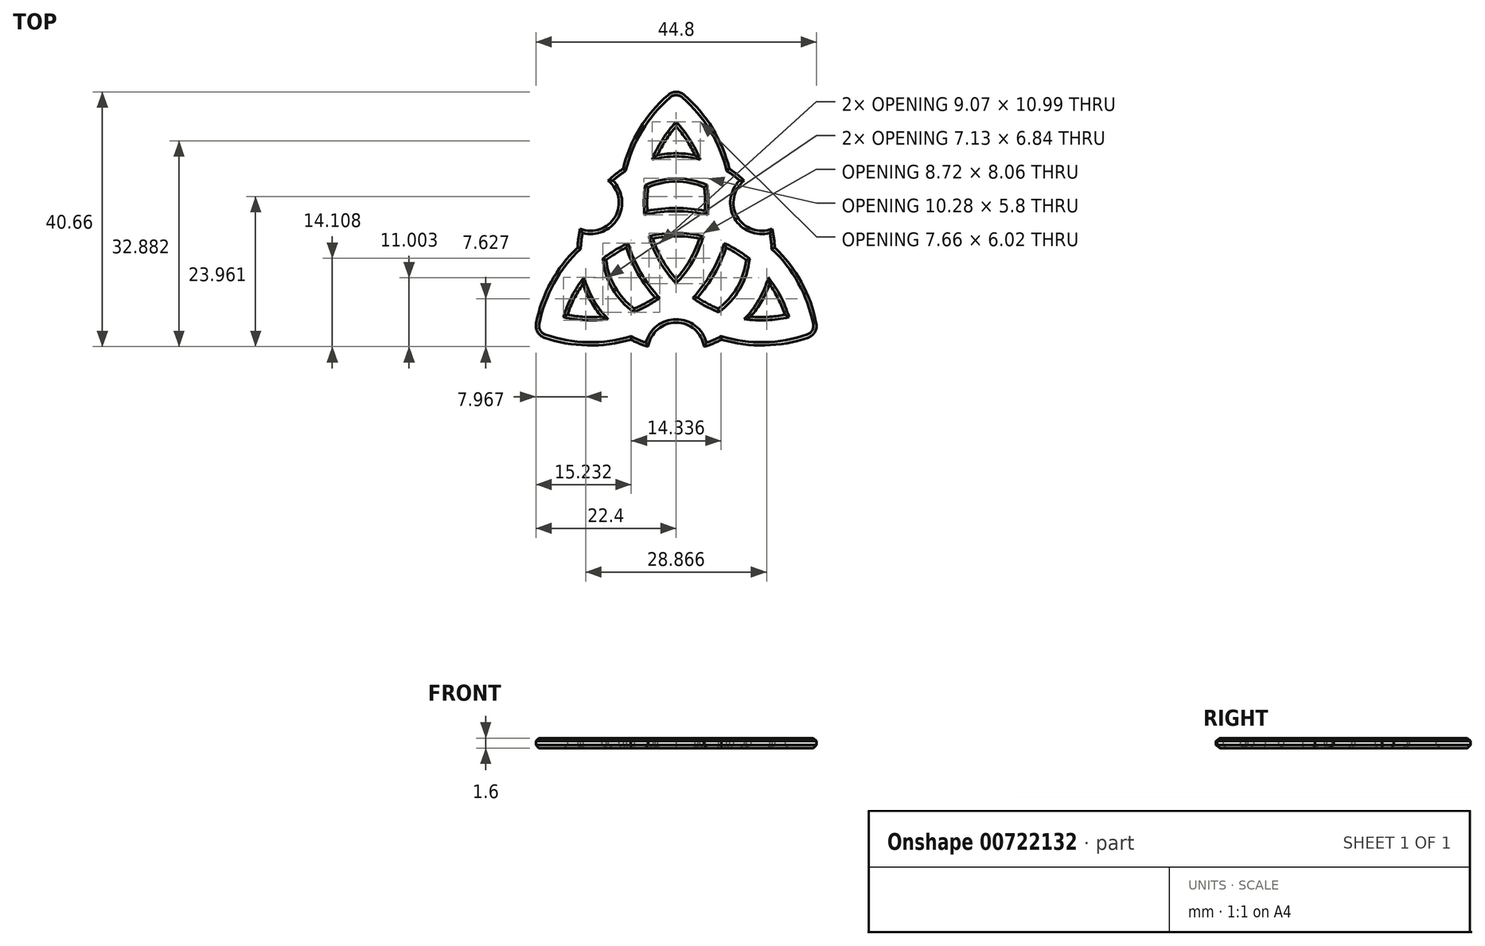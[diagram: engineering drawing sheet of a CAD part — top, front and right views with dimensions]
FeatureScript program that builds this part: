
annotation { "Feature Type Name" : "Feature", "Feature Type Description" : "" }
export const myFeature = defineFeature(function(context is Context, id is Id, definition is map)
    precondition{}
    {
        {
            var Q0;
            Q0=qCreatedBy(makeId("Top.planeOp"),FACE);
            var sketch = newSketch(context, id + "F0", { "sketchPlane" : qUnion([Q0])});
            skCircle(sketch, "E0", {"center": v(0, 0) * mm, "radius": 15.75 * mm});
            skCircle(sketch, "E1", {"center": v(0, 0) * mm, "radius": 11.25 * mm});
            skCircle(sketch, "E2", {"center": v(13.64, 7.88) * mm, "radius": 4.5 * mm});
            skCircle(sketch, "E3.1.0", {"center": v(-13.64, 7.88) * mm, "radius": 4.5 * mm});
            skCircle(sketch, "E3.2.0", {"center": v(0, -15.75) * mm, "radius": 4.5 * mm});
            skLineSegment(sketch, "E4", {"start": v(0, 0) * mm, "end": v(13.64, 7.88) * mm, "construction": true});
            skCircle(sketch, "E5", {"center": v(13.64, 7.88) * mm, "radius": 22.78 * mm});
            skCircle(sketch, "E6", {"center": v(13.64, 7.88) * mm, "radius": 18.28 * mm});
            skCircle(sketch, "E7.1.0", {"center": v(-13.64, 7.88) * mm, "radius": 18.28 * mm});
            skCircle(sketch, "E7.1.1", {"center": v(-13.64, 7.88) * mm, "radius": 22.78 * mm});
            skCircle(sketch, "E7.2.0", {"center": v(0, -15.75) * mm, "radius": 18.28 * mm});
            skCircle(sketch, "E7.2.1", {"center": v(0, -15.75) * mm, "radius": 22.78 * mm});
            skSolve(sketch);
        }
        {
            var Q0;
            {var subQ0=sQuery(id+"F0.wireOp",EDGE,"E7.2.0");var subQ1=sQuery(id+"F0.wireOp",EDGE,"E7.1.0");var subQ2=makeQuery(id+"F0.imprint","INTERSECT",VERTEX,{"disambiguationData":[OD(1.0)],"derivedFrom":[subQ1,subQ0]});Q0=makeQuery(id+"F0.imprint","IMPRINT",FACE,{"disambiguationData":[TD([[makeQuery(id+"F0.imprint","IMPRINT",EDGE,{"disambiguationData":[TD([[subQ2,-1.0]])],"derivedFrom":subQ1}),-1.0]])]});}
            var Q1;
            {var subQ0=sQuery(id+"F0.wireOp",EDGE,"E7.2.1");var subQ1=sQuery(id+"F0.wireOp",EDGE,"E1");var subQ2=makeQuery(id+"F0.imprint","INTERSECT",VERTEX,{"disambiguationData":[OD(0.0)],"derivedFrom":[subQ1,subQ0]});Q1=makeQuery(id+"F0.imprint","IMPRINT",FACE,{"disambiguationData":[TD([[makeQuery(id+"F0.imprint","IMPRINT",EDGE,{"disambiguationData":[TD([[subQ2,1.0]])],"derivedFrom":subQ1}),1.0]])]});}
            var Q2;
            {var subQ0=sQuery(id+"F0.wireOp",EDGE,"E7.2.1");var subQ1=sQuery(id+"F0.wireOp",EDGE,"E0");var subQ2=makeQuery(id+"F0.imprint","INTERSECT",VERTEX,{"disambiguationData":[OD(0.0)],"derivedFrom":[subQ1,subQ0]});Q2=makeQuery(id+"F0.imprint","IMPRINT",FACE,{"disambiguationData":[TD([[makeQuery(id+"F0.imprint","IMPRINT",EDGE,{"disambiguationData":[TD([[subQ2,1.0]])],"derivedFrom":subQ1}),1.0]])]});}
            var Q3;
            {var subQ0=sQuery(id+"F0.wireOp",EDGE,"E7.2.1");var subQ1=sQuery(id+"F0.wireOp",EDGE,"E0");var subQ2=makeQuery(id+"F0.imprint","INTERSECT",VERTEX,{"disambiguationData":[OD(0.0)],"derivedFrom":[subQ1,subQ0]});Q3=makeQuery(id+"F0.imprint","IMPRINT",FACE,{"disambiguationData":[TD([[makeQuery(id+"F0.imprint","IMPRINT",EDGE,{"disambiguationData":[TD([[subQ2,1.0]])],"derivedFrom":subQ1}),-1.0]])]});}
            var Q4;
            {var subQ0=sQuery(id+"F0.wireOp",EDGE,"E7.2.1");var subQ1=sQuery(id+"F0.wireOp",EDGE,"E5");var subQ2=makeQuery(id+"F0.imprint","INTERSECT",VERTEX,{"disambiguationData":[OD(0.0)],"derivedFrom":[subQ1,subQ0]});Q4=makeQuery(id+"F0.imprint","IMPRINT",FACE,{"disambiguationData":[TD([[makeQuery(id+"F0.imprint","IMPRINT",EDGE,{"disambiguationData":[TD([[subQ2,1.0]])],"derivedFrom":subQ1}),1.0]])]});}
            var Q5;
            {var subQ0=sQuery(id+"F0.wireOp",EDGE,"E5");var subQ1=sQuery(id+"F0.wireOp",EDGE,"E0");var subQ2=makeQuery(id+"F0.imprint","INTERSECT",VERTEX,{"disambiguationData":[OD(1.0)],"derivedFrom":[subQ1,subQ0]});Q5=makeQuery(id+"F0.imprint","IMPRINT",FACE,{"disambiguationData":[TD([[makeQuery(id+"F0.imprint","IMPRINT",EDGE,{"disambiguationData":[TD([[subQ2,-1.0]])],"derivedFrom":subQ1}),-1.0]])]});}
            var Q6;
            {var subQ0=sQuery(id+"F0.wireOp",EDGE,"E5");var subQ1=sQuery(id+"F0.wireOp",EDGE,"E0");var subQ2=makeQuery(id+"F0.imprint","INTERSECT",VERTEX,{"disambiguationData":[OD(1.0)],"derivedFrom":[subQ1,subQ0]});Q6=makeQuery(id+"F0.imprint","IMPRINT",FACE,{"disambiguationData":[TD([[makeQuery(id+"F0.imprint","IMPRINT",EDGE,{"disambiguationData":[TD([[subQ2,-1.0]])],"derivedFrom":subQ1}),1.0]])]});}
            var Q7;
            {var subQ0=sQuery(id+"F0.wireOp",EDGE,"E5");var subQ1=sQuery(id+"F0.wireOp",EDGE,"E1");var subQ2=makeQuery(id+"F0.imprint","INTERSECT",VERTEX,{"disambiguationData":[OD(1.0)],"derivedFrom":[subQ1,subQ0]});Q7=makeQuery(id+"F0.imprint","IMPRINT",FACE,{"disambiguationData":[TD([[makeQuery(id+"F0.imprint","IMPRINT",EDGE,{"disambiguationData":[TD([[subQ2,-1.0]])],"derivedFrom":subQ1}),1.0]])]});}
            var Q8;
            {var subQ0=sQuery(id+"F0.wireOp",EDGE,"E3.2.0");var subQ1=sQuery(id+"F0.wireOp",EDGE,"E0");var subQ2=makeQuery(id+"F0.imprint","INTERSECT",VERTEX,{"disambiguationData":[OD(1.0)],"derivedFrom":[subQ1,subQ0]});Q8=makeQuery(id+"F0.imprint","IMPRINT",FACE,{"disambiguationData":[TD([[makeQuery(id+"F0.imprint","IMPRINT",EDGE,{"disambiguationData":[TD([[subQ2,-1.0]])],"derivedFrom":subQ1}),1.0]])]});}
            var Q9;
            {var subQ0=sQuery(id+"F0.wireOp",EDGE,"E7.1.1");var subQ1=sQuery(id+"F0.wireOp",EDGE,"E0");var subQ2=makeQuery(id+"F0.imprint","INTERSECT",VERTEX,{"disambiguationData":[OD(1.0)],"derivedFrom":[subQ1,subQ0]});Q9=makeQuery(id+"F0.imprint","IMPRINT",FACE,{"disambiguationData":[TD([[makeQuery(id+"F0.imprint","IMPRINT",EDGE,{"disambiguationData":[TD([[subQ2,-1.0]])],"derivedFrom":subQ1}),1.0]])]});}
            var Q10;
            {var subQ1=sQuery(id+"F0.wireOp",EDGE,"E0");var subQ4=sQuery(id+"F0.wireOp",EDGE,"E7.1.0");var subQ5=makeQuery(id+"F0.imprint","INTERSECT",VERTEX,{"disambiguationData":[OD(1.0)],"derivedFrom":[subQ1,subQ4]});Q10=makeQuery(id+"F0.imprint","IMPRINT",FACE,{"disambiguationData":[TD([[makeQuery(id+"F0.imprint","IMPRINT",EDGE,{"disambiguationData":[TD([[subQ5,-1.0]])],"derivedFrom":subQ1}),1.0]])]});}
            var Q11;
            {var subQ0=sQuery(id+"F0.wireOp",EDGE,"E3.1.0");var subQ1=sQuery(id+"F0.wireOp",EDGE,"E0");var subQ2=makeQuery(id+"F0.imprint","INTERSECT",VERTEX,{"disambiguationData":[OD(1.0)],"derivedFrom":[subQ1,subQ0]});Q11=makeQuery(id+"F0.imprint","IMPRINT",FACE,{"disambiguationData":[TD([[makeQuery(id+"F0.imprint","IMPRINT",EDGE,{"disambiguationData":[TD([[subQ2,-1.0]])],"derivedFrom":subQ1}),1.0]])]});}
            var Q12;
            {var subQ0=sQuery(id+"F0.wireOp",EDGE,"E5");var subQ1=sQuery(id+"F0.wireOp",EDGE,"E0");var subQ2=makeQuery(id+"F0.imprint","INTERSECT",VERTEX,{"disambiguationData":[OD(0.0)],"derivedFrom":[subQ1,subQ0]});Q12=makeQuery(id+"F0.imprint","IMPRINT",FACE,{"disambiguationData":[TD([[makeQuery(id+"F0.imprint","IMPRINT",EDGE,{"disambiguationData":[TD([[subQ2,-1.0]])],"derivedFrom":subQ1}),1.0]])]});}
            var Q13;
            {var subQ4=sQuery(id+"F0.wireOp",EDGE,"E6");var subQ6=sQuery(id+"F0.wireOp",EDGE,"E0");var subQ8=makeQuery(id+"F0.imprint","INTERSECT",VERTEX,{"disambiguationData":[OD(0.0)],"derivedFrom":[subQ6,subQ4]});Q13=makeQuery(id+"F0.imprint","IMPRINT",FACE,{"disambiguationData":[TD([[makeQuery(id+"F0.imprint","IMPRINT",EDGE,{"disambiguationData":[TD([[subQ8,-1.0]])],"derivedFrom":subQ6}),1.0]])]});}
            var Q14;
            {var subQ0=sQuery(id+"F0.wireOp",EDGE,"E7.1.0");var subQ1=sQuery(id+"F0.wireOp",EDGE,"E0");var subQ2=makeQuery(id+"F0.imprint","INTERSECT",VERTEX,{"disambiguationData":[OD(0.0)],"derivedFrom":[subQ1,subQ0]});Q14=makeQuery(id+"F0.imprint","IMPRINT",FACE,{"disambiguationData":[TD([[makeQuery(id+"F0.imprint","IMPRINT",EDGE,{"disambiguationData":[TD([[subQ2,-1.0]])],"derivedFrom":subQ1}),1.0]])]});}
            var Q15;
            {var subQ1=sQuery(id+"F0.wireOp",EDGE,"E0");var subQ5=sQuery(id+"F0.wireOp",EDGE,"E7.1.1");var subQ8=makeQuery(id+"F0.imprint","INTERSECT",VERTEX,{"disambiguationData":[OD(0.0)],"derivedFrom":[subQ1,subQ5]});Q15=makeQuery(id+"F0.imprint","IMPRINT",FACE,{"disambiguationData":[TD([[makeQuery(id+"F0.imprint","IMPRINT",EDGE,{"disambiguationData":[TD([[subQ8,-1.0]])],"derivedFrom":subQ1}),1.0]])]});}
            var Q16;
            {var subQ0=sQuery(id+"F0.wireOp",EDGE,"E2");var subQ1=sQuery(id+"F0.wireOp",EDGE,"E0");var subQ2=makeQuery(id+"F0.imprint","INTERSECT",VERTEX,{"disambiguationData":[OD(1.0)],"derivedFrom":[subQ1,subQ0]});Q16=makeQuery(id+"F0.imprint","IMPRINT",FACE,{"disambiguationData":[TD([[makeQuery(id+"F0.imprint","IMPRINT",EDGE,{"disambiguationData":[TD([[subQ2,-1.0]])],"derivedFrom":subQ1}),1.0]])]});}
            var Q17;
            {var subQ0=sQuery(id+"F0.wireOp",EDGE,"E2");var subQ1=sQuery(id+"F0.wireOp",EDGE,"E0");var subQ2=makeQuery(id+"F0.imprint","INTERSECT",VERTEX,{"disambiguationData":[OD(0.0)],"derivedFrom":[subQ1,subQ0]});Q17=makeQuery(id+"F0.imprint","IMPRINT",FACE,{"disambiguationData":[TD([[makeQuery(id+"F0.imprint","IMPRINT",EDGE,{"disambiguationData":[TD([[subQ2,1.0]])],"derivedFrom":subQ1}),1.0]])]});}
            var Q18;
            {var subQ0=sQuery(id+"F0.wireOp",EDGE,"E6");var subQ1=sQuery(id+"F0.wireOp",EDGE,"E0");var subQ2=makeQuery(id+"F0.imprint","INTERSECT",VERTEX,{"disambiguationData":[OD(1.0)],"derivedFrom":[subQ1,subQ0]});Q18=makeQuery(id+"F0.imprint","IMPRINT",FACE,{"disambiguationData":[TD([[makeQuery(id+"F0.imprint","IMPRINT",EDGE,{"disambiguationData":[TD([[subQ2,-1.0]])],"derivedFrom":subQ1}),1.0]])]});}
            var Q19;
            {var subQ0=sQuery(id+"F0.wireOp",EDGE,"E7.1.0");var subQ1=sQuery(id+"F0.wireOp",EDGE,"E6");var subQ2=makeQuery(id+"F0.imprint","INTERSECT",VERTEX,{"disambiguationData":[OD(1.0)],"derivedFrom":[subQ1,subQ0]});Q19=makeQuery(id+"F0.imprint","IMPRINT",FACE,{"disambiguationData":[TD([[makeQuery(id+"F0.imprint","IMPRINT",EDGE,{"disambiguationData":[TD([[subQ2,-1.0]])],"derivedFrom":subQ1}),1.0]])]});}
            var Q20;
            {var subQ0=sQuery(id+"F0.wireOp",EDGE,"E7.1.0");var subQ1=sQuery(id+"F0.wireOp",EDGE,"E5");var subQ2=makeQuery(id+"F0.imprint","INTERSECT",VERTEX,{"disambiguationData":[OD(1.0)],"derivedFrom":[subQ1,subQ0]});Q20=makeQuery(id+"F0.imprint","IMPRINT",FACE,{"disambiguationData":[TD([[makeQuery(id+"F0.imprint","IMPRINT",EDGE,{"disambiguationData":[TD([[subQ2,-1.0]])],"derivedFrom":subQ1}),1.0]])]});}
            var Q21;
            {var subQ0=sQuery(id+"F0.wireOp",EDGE,"E7.1.0");var subQ1=sQuery(id+"F0.wireOp",EDGE,"E1");var subQ2=makeQuery(id+"F0.imprint","INTERSECT",VERTEX,{"disambiguationData":[OD(1.0)],"derivedFrom":[subQ1,subQ0]});Q21=makeQuery(id+"F0.imprint","IMPRINT",FACE,{"disambiguationData":[TD([[makeQuery(id+"F0.imprint","IMPRINT",EDGE,{"disambiguationData":[TD([[subQ2,-1.0]])],"derivedFrom":subQ1}),1.0]])]});}
            var Q22;
            {var subQ0=sQuery(id+"F0.wireOp",EDGE,"E7.2.0");var subQ1=sQuery(id+"F0.wireOp",EDGE,"E5");var subQ2=makeQuery(id+"F0.imprint","INTERSECT",VERTEX,{"disambiguationData":[OD(0.0)],"derivedFrom":[subQ1,subQ0]});Q22=makeQuery(id+"F0.imprint","IMPRINT",FACE,{"disambiguationData":[TD([[makeQuery(id+"F0.imprint","IMPRINT",EDGE,{"disambiguationData":[TD([[subQ2,-1.0]])],"derivedFrom":subQ1}),1.0]])]});}
            var Q23;
            {var subQ0=sQuery(id+"F0.wireOp",EDGE,"E7.2.1");var subQ1=sQuery(id+"F0.wireOp",EDGE,"E5");var subQ2=makeQuery(id+"F0.imprint","INTERSECT",VERTEX,{"disambiguationData":[OD(1.0)],"derivedFrom":[subQ1,subQ0]});Q23=makeQuery(id+"F0.imprint","IMPRINT",FACE,{"disambiguationData":[TD([[makeQuery(id+"F0.imprint","IMPRINT",EDGE,{"disambiguationData":[TD([[subQ2,-1.0]])],"derivedFrom":subQ1}),1.0]])]});}
            var Q24;
            {var subQ0=sQuery(id+"F0.wireOp",EDGE,"E6");var subQ1=sQuery(id+"F0.wireOp",EDGE,"E1");var subQ2=makeQuery(id+"F0.imprint","INTERSECT",VERTEX,{"disambiguationData":[OD(0.0)],"derivedFrom":[subQ1,subQ0]});Q24=makeQuery(id+"F0.imprint","IMPRINT",FACE,{"disambiguationData":[TD([[makeQuery(id+"F0.imprint","IMPRINT",EDGE,{"disambiguationData":[TD([[subQ2,-1.0]])],"derivedFrom":subQ1}),1.0]])]});}
            var Q25;
            {var subQ0=sQuery(id+"F0.wireOp",EDGE,"E7.1.1");var subQ1=sQuery(id+"F0.wireOp",EDGE,"E1");var subQ2=makeQuery(id+"F0.imprint","INTERSECT",VERTEX,{"disambiguationData":[OD(0.0)],"derivedFrom":[subQ1,subQ0]});Q25=makeQuery(id+"F0.imprint","IMPRINT",FACE,{"disambiguationData":[TD([[makeQuery(id+"F0.imprint","IMPRINT",EDGE,{"disambiguationData":[TD([[subQ2,-1.0]])],"derivedFrom":subQ1}),1.0]])]});}
            var Q26;
            {var subQ0=sQuery(id+"F0.wireOp",EDGE,"E7.2.1");var subQ5=sQuery(id+"F0.wireOp",EDGE,"E0");var subQ8=makeQuery(id+"F0.imprint","INTERSECT",VERTEX,{"disambiguationData":[OD(1.0)],"derivedFrom":[subQ5,subQ0]});Q26=makeQuery(id+"F0.imprint","IMPRINT",FACE,{"disambiguationData":[TD([[makeQuery(id+"F0.imprint","IMPRINT",EDGE,{"disambiguationData":[TD([[subQ8,-1.0]])],"derivedFrom":subQ5}),1.0]])]});}
            var Q27;
            {var subQ0=sQuery(id+"F0.wireOp",EDGE,"E7.2.0");var subQ1=sQuery(id+"F0.wireOp",EDGE,"E0");var subQ2=makeQuery(id+"F0.imprint","INTERSECT",VERTEX,{"disambiguationData":[OD(0.0)],"derivedFrom":[subQ1,subQ0]});Q27=makeQuery(id+"F0.imprint","IMPRINT",FACE,{"disambiguationData":[TD([[makeQuery(id+"F0.imprint","IMPRINT",EDGE,{"disambiguationData":[TD([[subQ2,-1.0]])],"derivedFrom":subQ1}),1.0]])]});}
            var Q28;
            {var subQ0=sQuery(id+"F0.wireOp",EDGE,"E7.2.1");var subQ1=sQuery(id+"F0.wireOp",EDGE,"E1");var subQ2=makeQuery(id+"F0.imprint","INTERSECT",VERTEX,{"disambiguationData":[OD(1.0)],"derivedFrom":[subQ1,subQ0]});Q28=makeQuery(id+"F0.imprint","IMPRINT",FACE,{"disambiguationData":[TD([[makeQuery(id+"F0.imprint","IMPRINT",EDGE,{"disambiguationData":[TD([[subQ2,-1.0]])],"derivedFrom":subQ1}),1.0]])]});}
            var Q29;
            {var subQ0=sQuery(id+"F0.wireOp",EDGE,"E7.2.1");var subQ1=sQuery(id+"F0.wireOp",EDGE,"E6");var subQ2=makeQuery(id+"F0.imprint","INTERSECT",VERTEX,{"disambiguationData":[OD(0.0)],"derivedFrom":[subQ1,subQ0]});Q29=makeQuery(id+"F0.imprint","IMPRINT",FACE,{"disambiguationData":[TD([[makeQuery(id+"F0.imprint","IMPRINT",EDGE,{"disambiguationData":[TD([[subQ2,-1.0]])],"derivedFrom":subQ1}),1.0]])]});}
            var Q30;
            {var subQ0=sQuery(id+"F0.wireOp",EDGE,"E7.1.1");var subQ1=sQuery(id+"F0.wireOp",EDGE,"E0");var subQ2=makeQuery(id+"F0.imprint","INTERSECT",VERTEX,{"disambiguationData":[OD(0.0)],"derivedFrom":[subQ1,subQ0]});Q30=makeQuery(id+"F0.imprint","IMPRINT",FACE,{"disambiguationData":[TD([[makeQuery(id+"F0.imprint","IMPRINT",EDGE,{"disambiguationData":[TD([[subQ2,-1.0]])],"derivedFrom":subQ1}),-1.0]])]});}
            var Q31;
            {var subQ0=sQuery(id+"F0.wireOp",EDGE,"E7.1.1");var subQ1=sQuery(id+"F0.wireOp",EDGE,"E5");var subQ2=makeQuery(id+"F0.imprint","INTERSECT",VERTEX,{"disambiguationData":[OD(0.0)],"derivedFrom":[subQ1,subQ0]});Q31=makeQuery(id+"F0.imprint","IMPRINT",FACE,{"disambiguationData":[TD([[makeQuery(id+"F0.imprint","IMPRINT",EDGE,{"disambiguationData":[TD([[subQ2,-1.0]])],"derivedFrom":subQ1}),1.0]])]});}
            var Q32;
            {var subQ0=sQuery(id+"F0.wireOp",EDGE,"E6");var subQ1=sQuery(id+"F0.wireOp",EDGE,"E0");var subQ2=makeQuery(id+"F0.imprint","INTERSECT",VERTEX,{"disambiguationData":[OD(0.0)],"derivedFrom":[subQ1,subQ0]});Q32=makeQuery(id+"F0.imprint","IMPRINT",FACE,{"disambiguationData":[TD([[makeQuery(id+"F0.imprint","IMPRINT",EDGE,{"disambiguationData":[TD([[subQ2,-1.0]])],"derivedFrom":subQ1}),-1.0]])]});}
            var Q33;
            {var subQ0=sQuery(id+"F0.wireOp",EDGE,"E7.2.1");var subQ1=sQuery(id+"F0.wireOp",EDGE,"E0");var subQ2=makeQuery(id+"F0.imprint","INTERSECT",VERTEX,{"disambiguationData":[OD(1.0)],"derivedFrom":[subQ1,subQ0]});Q33=makeQuery(id+"F0.imprint","IMPRINT",FACE,{"disambiguationData":[TD([[makeQuery(id+"F0.imprint","IMPRINT",EDGE,{"disambiguationData":[TD([[subQ2,-1.0]])],"derivedFrom":subQ1}),-1.0]])]});}
            var Q34;
            {var subQ0=sQuery(id+"F0.wireOp",EDGE,"E7.2.0");var subQ1=sQuery(id+"F0.wireOp",EDGE,"E7.1.0");var subQ2=makeQuery(id+"F0.imprint","INTERSECT",VERTEX,{"disambiguationData":[OD(0.0)],"derivedFrom":[subQ1,subQ0]});Q34=makeQuery(id+"F0.imprint","IMPRINT",FACE,{"disambiguationData":[TD([[makeQuery(id+"F0.imprint","IMPRINT",EDGE,{"disambiguationData":[TD([[subQ2,1.0]])],"derivedFrom":subQ1}),-1.0]])]});}
            var Q35;
            {var subQ0=sQuery(id+"F0.wireOp",EDGE,"E7.1.0");var subQ1=sQuery(id+"F0.wireOp",EDGE,"E0");var subQ2=makeQuery(id+"F0.imprint","INTERSECT",VERTEX,{"disambiguationData":[OD(1.0)],"derivedFrom":[subQ1,subQ0]});Q35=makeQuery(id+"F0.imprint","IMPRINT",FACE,{"disambiguationData":[TD([[makeQuery(id+"F0.imprint","IMPRINT",EDGE,{"disambiguationData":[TD([[subQ2,-1.0]])],"derivedFrom":subQ1}),-1.0]])]});}
            var Q36;
            {var subQ0=sQuery(id+"F0.wireOp",EDGE,"E7.1.1");var subQ1=sQuery(id+"F0.wireOp",EDGE,"E1");var subQ2=makeQuery(id+"F0.imprint","INTERSECT",VERTEX,{"disambiguationData":[OD(1.0)],"derivedFrom":[subQ1,subQ0]});Q36=makeQuery(id+"F0.imprint","IMPRINT",FACE,{"disambiguationData":[TD([[makeQuery(id+"F0.imprint","IMPRINT",EDGE,{"disambiguationData":[TD([[subQ2,-1.0]])],"derivedFrom":subQ1}),1.0]])]});}
            var Q37;
            {var subQ0=sQuery(id+"F0.wireOp",EDGE,"E3.2.0");var subQ1=sQuery(id+"F0.wireOp",EDGE,"E1");var subQ2=makeQuery(id+"F0.imprint","INTERSECT",VERTEX,{"derivedFrom":[subQ1,subQ0]});Q37=makeQuery(id+"F0.imprint","IMPRINT",FACE,{"disambiguationData":[TD([[makeQuery(id+"F0.imprint","IMPRINT",EDGE,{"disambiguationData":[TD([[subQ2,-1.0]])],"derivedFrom":subQ1}),-1.0]])]});}
            var Q38;
            {var subQ0=sQuery(id+"F0.wireOp",EDGE,"E7.1.1");var subQ1=sQuery(id+"F0.wireOp",EDGE,"E1");var subQ2=makeQuery(id+"F0.imprint","INTERSECT",VERTEX,{"disambiguationData":[OD(1.0)],"derivedFrom":[subQ1,subQ0]});Q38=makeQuery(id+"F0.imprint","IMPRINT",FACE,{"disambiguationData":[TD([[makeQuery(id+"F0.imprint","IMPRINT",EDGE,{"disambiguationData":[TD([[subQ2,-1.0]])],"derivedFrom":subQ1}),-1.0]])]});}
            var Q39;
            {var subQ0=sQuery(id+"F0.wireOp",EDGE,"E1");var subQ1=makeQuery(id+"F0.imprint","INTERSECT",VERTEX,{"derivedFrom":[subQ0,sQuery(id+"F0.wireOp",EDGE,"E2")]});Q39=makeQuery(id+"F0.imprint","IMPRINT",FACE,{"disambiguationData":[TD([[makeQuery(id+"F0.imprint","IMPRINT",EDGE,{"disambiguationData":[TD([[subQ1,1.0]])],"derivedFrom":subQ0}),1.0]])]});}
            var Q40;
            {var subQ0=sQuery(id+"F0.wireOp",EDGE,"E2");var subQ1=sQuery(id+"F0.wireOp",EDGE,"E1");var subQ2=makeQuery(id+"F0.imprint","INTERSECT",VERTEX,{"derivedFrom":[subQ1,subQ0]});Q40=makeQuery(id+"F0.imprint","IMPRINT",FACE,{"disambiguationData":[TD([[makeQuery(id+"F0.imprint","IMPRINT",EDGE,{"disambiguationData":[TD([[subQ2,1.0]])],"derivedFrom":subQ1}),-1.0]])]});}
            var Q41;
            {var subQ0=sQuery(id+"F0.wireOp",EDGE,"E2");var subQ1=sQuery(id+"F0.wireOp",EDGE,"E1");var subQ2=makeQuery(id+"F0.imprint","INTERSECT",VERTEX,{"derivedFrom":[subQ1,subQ0]});Q41=makeQuery(id+"F0.imprint","IMPRINT",FACE,{"disambiguationData":[TD([[makeQuery(id+"F0.imprint","IMPRINT",EDGE,{"disambiguationData":[TD([[subQ2,-1.0]])],"derivedFrom":subQ1}),-1.0]])]});}
            var Q42;
            {var subQ0=sQuery(id+"F0.wireOp",EDGE,"E3.1.0");var subQ1=sQuery(id+"F0.wireOp",EDGE,"E1");var subQ2=makeQuery(id+"F0.imprint","INTERSECT",VERTEX,{"derivedFrom":[subQ1,subQ0]});Q42=makeQuery(id+"F0.imprint","IMPRINT",FACE,{"disambiguationData":[TD([[makeQuery(id+"F0.imprint","IMPRINT",EDGE,{"disambiguationData":[TD([[subQ2,-1.0]])],"derivedFrom":subQ1}),-1.0]])]});}
            var Q43;
            {var subQ0=sQuery(id+"F0.wireOp",EDGE,"E5");var subQ1=sQuery(id+"F0.wireOp",EDGE,"E1");var subQ2=makeQuery(id+"F0.imprint","INTERSECT",VERTEX,{"disambiguationData":[OD(0.0)],"derivedFrom":[subQ1,subQ0]});Q43=makeQuery(id+"F0.imprint","IMPRINT",FACE,{"disambiguationData":[TD([[makeQuery(id+"F0.imprint","IMPRINT",EDGE,{"disambiguationData":[TD([[subQ2,-1.0]])],"derivedFrom":subQ1}),1.0]])]});}
            var Q44;
            {var subQ0=sQuery(id+"F0.wireOp",EDGE,"E5");var subQ1=sQuery(id+"F0.wireOp",EDGE,"E1");var subQ2=makeQuery(id+"F0.imprint","INTERSECT",VERTEX,{"disambiguationData":[OD(0.0)],"derivedFrom":[subQ1,subQ0]});Q44=makeQuery(id+"F0.imprint","IMPRINT",FACE,{"disambiguationData":[TD([[makeQuery(id+"F0.imprint","IMPRINT",EDGE,{"disambiguationData":[TD([[subQ2,-1.0]])],"derivedFrom":subQ1}),-1.0]])]});}
            extrude(context, id + "F1", {"entities" : qUnion([Q0, Q1, Q2, Q3, Q4, Q5, Q6, Q7, Q8, Q9, Q10, Q11, Q12, Q13, Q14, Q15, Q16, Q17, Q18, Q19, Q20, Q21, Q22, Q23, Q24, Q25, Q26, Q27, Q28, Q29, Q30, Q31, Q32, Q33, Q34, Q35, Q36, Q37, Q38, Q39, Q40, Q41, Q42, Q43, Q44]), "depth" : 1.6 * mm, "offsetDistance" : 25 * mm});
        }
        {
            var Q0;
            {var subQ0=sQuery(id+"F0.wireOp",EDGE,"E7.2.1");var subQ1=sQuery(id+"F0.wireOp",EDGE,"E7.1.1");Q0=makeQuery(id+"F1.opExtrude","SWEPT_EDGE",EDGE,{"disambiguationData":[OSD([subQ1,subQ0]),TDD([makeQuery(id+"F0.imprint","INTERSECT",VERTEX,{"disambiguationData":[OD(0.0)],"derivedFrom":[subQ1,subQ0]})])]});}
            var Q1;
            {var subQ0=sQuery(id+"F0.wireOp",EDGE,"E7.2.1");var subQ1=sQuery(id+"F0.wireOp",EDGE,"E5");Q1=makeQuery(id+"F1.opExtrude","SWEPT_EDGE",EDGE,{"disambiguationData":[OSD([subQ1,subQ0]),TDD([makeQuery(id+"F0.imprint","INTERSECT",VERTEX,{"disambiguationData":[OD(0.0)],"derivedFrom":[subQ1,subQ0]})])]});}
            var Q2;
            {var subQ0=sQuery(id+"F0.wireOp",EDGE,"E7.1.1");var subQ1=sQuery(id+"F0.wireOp",EDGE,"E5");Q2=makeQuery(id+"F1.opExtrude","SWEPT_EDGE",EDGE,{"disambiguationData":[OSD([subQ1,subQ0]),TDD([makeQuery(id+"F0.imprint","INTERSECT",VERTEX,{"disambiguationData":[OD(0.0)],"derivedFrom":[subQ1,subQ0]})])]});}
            fillet(context, id + "F2", {"entities" : qUnion([Q0, Q1, Q2]), "radius" : 2 * mm, "tangentPropagation" : true, "allowEdgeOverflow" : false});
        }
        {
            var Q0;
            Q0=makeQuery(id+"F1.opExtrude","CAP_FACE",FACE,{"disambiguationData":[OSD([sQuery(id+"F0.wireOp",EDGE,"E0"),sQuery(id+"F0.wireOp",EDGE,"E1"),sQuery(id+"F0.wireOp",EDGE,"E2"),sQuery(id+"F0.wireOp",EDGE,"E3.1.0"),sQuery(id+"F0.wireOp",EDGE,"E3.2.0"),sQuery(id+"F0.wireOp",EDGE,"E5"),sQuery(id+"F0.wireOp",EDGE,"E6"),sQuery(id+"F0.wireOp",EDGE,"E7.1.0"),sQuery(id+"F0.wireOp",EDGE,"E7.1.1"),sQuery(id+"F0.wireOp",EDGE,"E7.2.0"),sQuery(id+"F0.wireOp",EDGE,"E7.2.1")])],"isStart":false});
            var Q1;
            Q1=makeQuery(id+"F1.opExtrude","CAP_FACE",FACE,{"disambiguationData":[OSD([sQuery(id+"F0.wireOp",EDGE,"E0"),sQuery(id+"F0.wireOp",EDGE,"E1"),sQuery(id+"F0.wireOp",EDGE,"E2"),sQuery(id+"F0.wireOp",EDGE,"E3.1.0"),sQuery(id+"F0.wireOp",EDGE,"E3.2.0"),sQuery(id+"F0.wireOp",EDGE,"E5"),sQuery(id+"F0.wireOp",EDGE,"E6"),sQuery(id+"F0.wireOp",EDGE,"E7.1.0"),sQuery(id+"F0.wireOp",EDGE,"E7.1.1"),sQuery(id+"F0.wireOp",EDGE,"E7.2.0"),sQuery(id+"F0.wireOp",EDGE,"E7.2.1")])],"isStart":true});
            chamfer(context, id + "F3", {"entities" : qUnion([Q0, Q1]), "chamferType" : ChamferType.TWO_OFFSETS, "width1" : 0.5 * mm, "oppositeDirection" : false, "width2" : 0.5 * mm, "tangentPropagation" : true});
        }
    });
